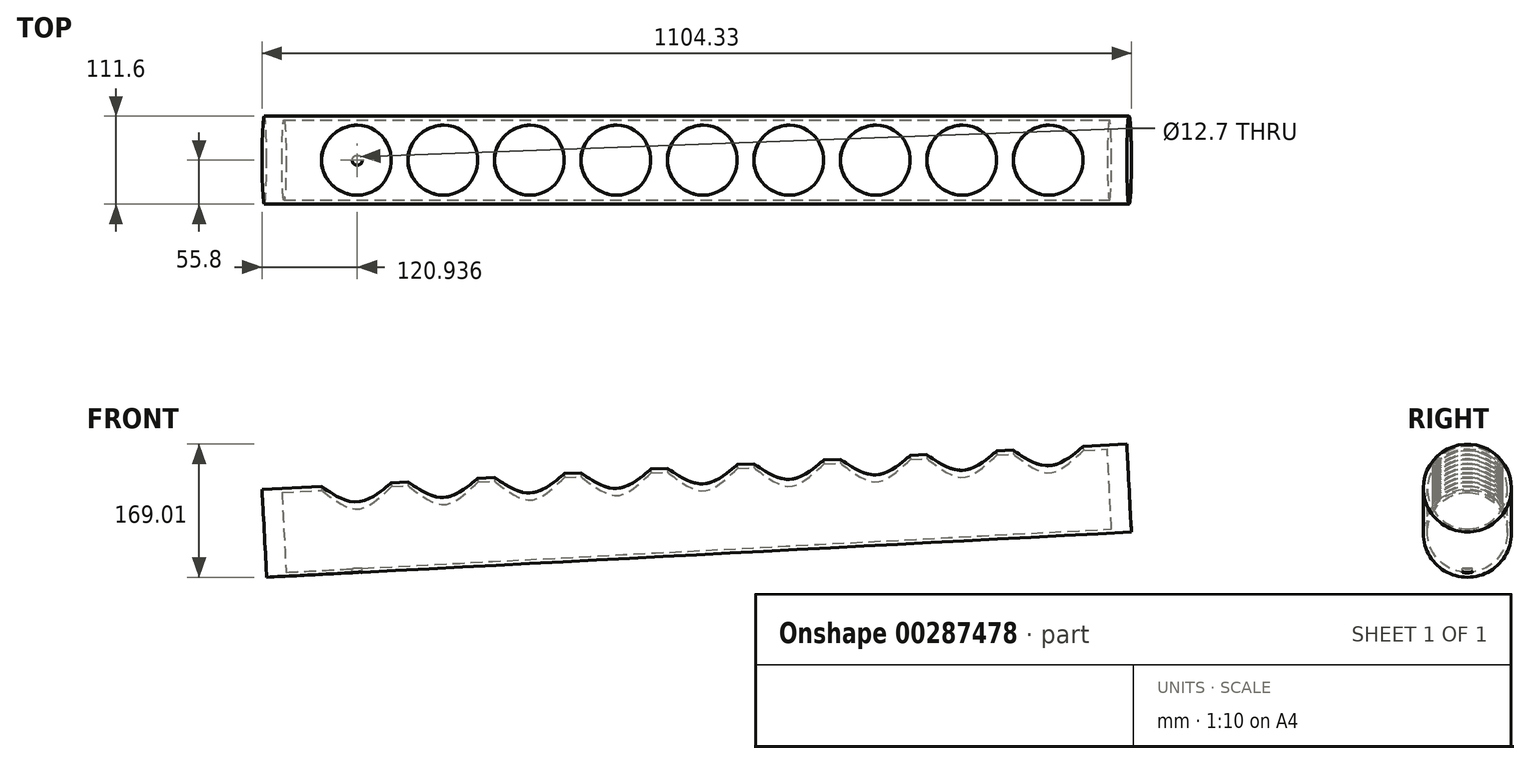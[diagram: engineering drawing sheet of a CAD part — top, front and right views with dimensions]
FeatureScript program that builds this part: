
annotation { "Feature Type Name" : "Feature", "Feature Type Description" : "" }
export const myFeature = defineFeature(function(context is Context, id is Id, definition is map)
    precondition{}
    {
        {
            var Q0;
            Q0=qCreatedBy(makeId("Right.planeOp"),FACE);
            var sketch = newSketch(context, id + "F0", { "sketchPlane" : qUnion([Q0])});
            skCircle(sketch, "E0", {"center": v(0, 0) * mm, "radius": 50.8 * mm});
            skCircle(sketch, "E1.0", {"center": v(0, 0) * mm, "radius": 55.8 * mm});
            skLineSegment(sketch, "E2", {"start": v(-50.8, 0) * mm, "end": v(50.8, 0) * mm, "construction": true});
            skSolve(sketch);
        }
        {
            var Q0;
            Q0=qSketchRegion(id+"F0",true);
            extrude(context, id + "F1", {"entities" : qUnion([Q0]), "oppositeDirection" : true, "depth" : 1100 * mm});
        }
        {
            var Q0;
            Q0=qCreatedBy(makeId("Right.planeOp"),FACE);
            var sketch = newSketch(context, id + "F2", { "sketchPlane" : qUnion([Q0])});
            skLineSegment(sketch, "E3", {"start": v(-70.21, 0) * mm, "end": v(69.9, 0) * mm, "construction": true});
            skSolve(sketch);
        }
        {
            var Q0;
            Q0=qCreatedBy(makeId("Top.planeOp"),FACE);
            var sketch = newSketch(context, id + "F3", { "sketchPlane" : qUnion([Q0])});
            skCircle(sketch, "E4", {"center": v(-100, 0) * mm, "radius": 44.45 * mm});
            skCircle(sketch, "E5.1.0.0", {"center": v(-210, 0) * mm, "radius": 44.45 * mm});
            skCircle(sketch, "E5.2.0.0", {"center": v(-320, 0) * mm, "radius": 44.45 * mm});
            skCircle(sketch, "E5.3.0.0", {"center": v(-430, 0) * mm, "radius": 44.45 * mm});
            skCircle(sketch, "E5.4.0.0", {"center": v(-540, 0) * mm, "radius": 44.45 * mm});
            skCircle(sketch, "E5.5.0.0", {"center": v(-650, 0) * mm, "radius": 44.45 * mm});
            skCircle(sketch, "E5.6.0.0", {"center": v(-760, 0) * mm, "radius": 44.45 * mm});
            skCircle(sketch, "E5.7.0.0", {"center": v(-870, 0) * mm, "radius": 44.45 * mm});
            skCircle(sketch, "E5.8.0.0", {"center": v(-980, 0) * mm, "radius": 44.45 * mm});
            skLineSegment(sketch, "E5.direction1", {"start": v(-100, 0) * mm, "end": v(-210, 0) * mm, "construction": true});
            skSolve(sketch);
        }
        {
            var Q0;
            Q0=qSketchRegion(id+"F3",true);
            extrude(context, id + "F4", {"entities" : qUnion([Q0]), "operationType" : NewBodyOperationType.REMOVE, "endBound" : BoundingType.THROUGH_ALL, "depth" : 25 * mm});
        }
        {
            var Q0;
            Q0=makeQuery(id+"F1.opExtrude","SWEPT_BODY",BODY,{"disambiguationData":[OSD([sQuery(id+"F0.wireOp",EDGE,"E0"),sQuery(id+"F0.wireOp",EDGE,"E1.0")])]});
            var Q1;
            Q1=sQuery(id+"F2.wireOp",EDGE,"E3");
            transform(context, id + "F5", {"entities" : qUnion([Q0]), "transformType" : TransformType.ROTATION, "transformAxis" : qUnion([Q1]), "angle" : 3 * degree, "oppositeDirection" : true, "makeCopy" : false});
        }
        {
            var Q0;
            Q0=makeQuery(id+"F1.opExtrude","CAP_FACE",FACE,{"disambiguationData":[OSD([sQuery(id+"F0.wireOp",EDGE,"E0"),sQuery(id+"F0.wireOp",EDGE,"E1.0")])],"isStart":false});
            var sketch = newSketch(context, id + "F6", { "sketchPlane" : qUnion([Q0])});
            skCircle(sketch, "E6", {"center": v(0, 0) * mm, "radius": 54.33 * mm});
            skSolve(sketch);
        }
        {
            var Q0;
            Q0=qSketchRegion(id+"F6",true);
            extrude(context, id + "F7", {"entities" : qUnion([Q0]), "operationType" : NewBodyOperationType.ADD, "oppositeDirection" : true, "depth" : 25 * mm});
        }
        {
            var Q0;
            Q0=makeQuery(id+"F1.opExtrude","CAP_FACE",FACE,{"disambiguationData":[OSD([sQuery(id+"F0.wireOp",EDGE,"E0"),sQuery(id+"F0.wireOp",EDGE,"E1.0")])],"isStart":true});
            var sketch = newSketch(context, id + "F8", { "sketchPlane" : qUnion([Q0])});
            skCircle(sketch, "E7", {"center": v(0, 0) * mm, "radius": 53.8 * mm});
            skSolve(sketch);
        }
        {
            var Q0;
            Q0=qSketchRegion(id+"F8",true);
            extrude(context, id + "F9", {"entities" : qUnion([Q0]), "operationType" : NewBodyOperationType.ADD, "oppositeDirection" : true, "depth" : 25 * mm});
        }
        {
            var Q0;
            Q0=qCreatedBy(makeId("Top.planeOp"),FACE);
            var sketch = newSketch(context, id + "F10", { "sketchPlane" : qUnion([Q0])});
            skCircle(sketch, "E8", {"center": v(-980.47, 0) * mm, "radius": 6.35 * mm});
            skSolve(sketch);
        }
        {
            var Q0;
            Q0=qSketchRegion(id+"F10",true);
            extrude(context, id + "F11", {"entities" : qUnion([Q0]), "operationType" : NewBodyOperationType.REMOVE, "endBound" : BoundingType.THROUGH_ALL, "oppositeDirection" : true, "depth" : 25 * mm});
        }
    });
